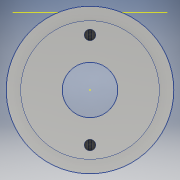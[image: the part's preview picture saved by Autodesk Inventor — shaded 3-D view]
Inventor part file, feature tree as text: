
AUTODESK INVENTOR PART (.ipt)
format: ipt  version: 2017 (Build 210142000, 142)  size: 210,944 bytes
history: native  units: in
note: dims shown in document units (in); Inventor stores cm internally (conversion verified against a paired STEP export)
features: sketch x9, hole x5, plane x4, revolve x1, fillet x1, extrude x1, chamfer x1
ambient origin geometry x8: Origin, YZ Plane, XZ Plane, XY Plane, X Axis, Y Axis, Z Axis, Center Point
bodies: Solid1 (feature_tree)
feature tree (22):
  revolve  "Revolution1"  [1 undecoded]
  hole  "Hole1"  [1 undecoded]
  fillet  "Fillet1"  Radius=1.4975in
  extrude  "Extrusion1"  Depth=2.376in
  sketch  "Sketch5"  dims[d15=0.25in d16=0.75in d17=0.375in d18=0.25in d19=0.5635in d20=0.4in d21=0.0in d22=0.125in]
  sketch  "Sketch6"  dims[d23=1.995in d24=0.3125in d25=0.0in]
  plane  "Work Plane1"
  sketch  "Sketch7"  dims[d26=1.679in d27=-1.679in]
  plane  "Work Plane2"
  sketch  "Sketch9"  dims[d28=-1.679in d29=1.679in]
  plane  "Work Plane3"
  sketch  "Sketch10"  dims[d30=0.13in d31=0.328in d32=0.375in d33=0.25in d34=0.5635in d35=0.484in d36=0.8108in]
  plane  "Work Plane4"
  sketch  "Sketch11"  dims[d37=0.13in d38=0.328in d39=0.375in d40=0.25in d41=0.5635in d42=0.484in d43=0.8108in d44=0.13in d45=0.328in d46=0.375in d47=0.25in d48=0.5635in d49=0.484in d50=0.8108in d51=1.1875in d52=0.328in d53=0.375in d54=0.25in d55=0.5635in d56=0.484in d57=0.8108in d58=0.01in d59=0.125in d60=45.0deg]
  hole  "Hole2"  [1 undecoded]
  hole  "Hole3"  [1 undecoded]
  hole  "Hole4"  [1 undecoded]
  hole  "Hole5"  [1 undecoded]
  chamfer  "Chamfer1"  Distance=0.125in Angle=45.0deg
  sketch  "Sketch1"  dims[d1=0.5in d3=0.147in d5=0.195in d8=0.691in d9=1.668in]
  sketch  "Sketch2"  dims[d10=1.814in d11=0.062in d12=1.4975in]
  sketch  "Sketch3"  dims[d13=90.0deg d14=2.376in]
note: 6 required parameter values undecoded (feature->parameter linkage not recoverable at this tier; creation-order binding heuristic only, values carry confidence <= 0.55)